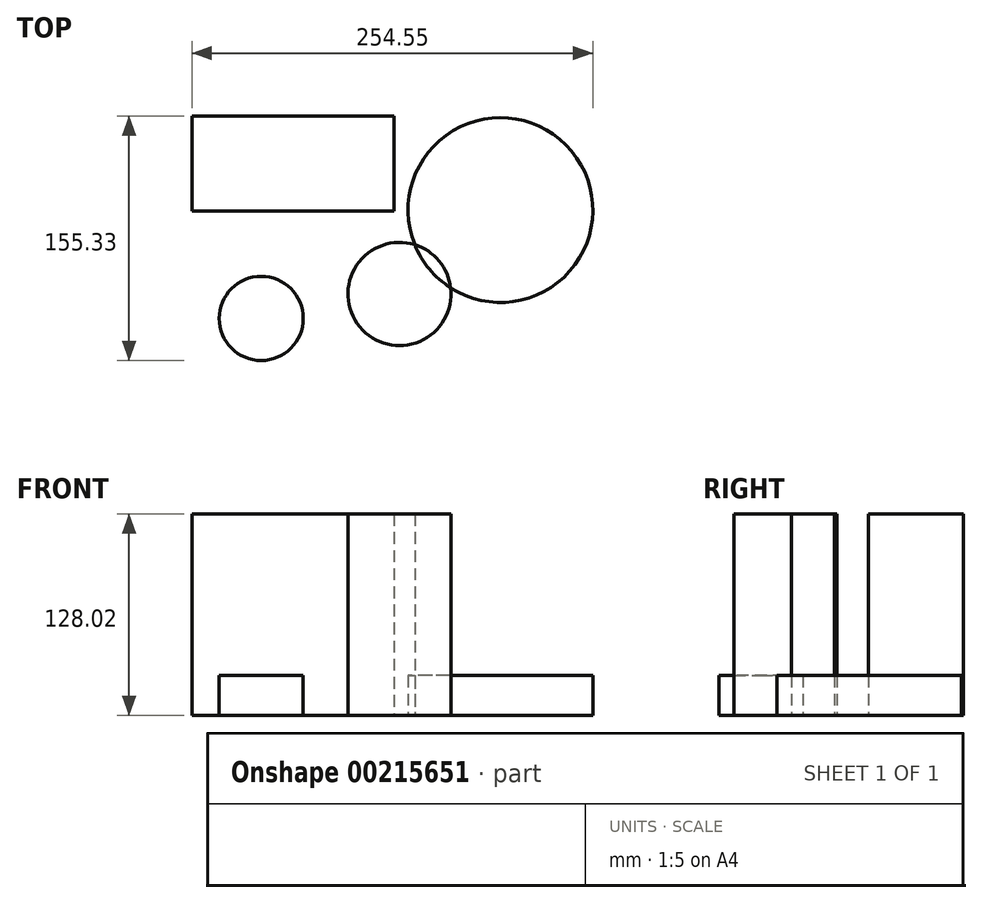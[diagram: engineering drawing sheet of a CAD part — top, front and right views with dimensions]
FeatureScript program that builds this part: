
annotation { "Feature Type Name" : "Feature", "Feature Type Description" : "" }
export const myFeature = defineFeature(function(context is Context, id is Id, definition is map)
    precondition{}
    {
        {
            var Q0;
            Q0=qCreatedBy(makeId("Top.planeOp"),FACE);
            var sketch = newSketch(context, id + "F0", { "sketchPlane" : qUnion([Q0])});
            skLineSegment(sketch, "E0.bottom", {"start": v(40.48, 26.16) * mm, "end": v(-87.82, 26.16) * mm});
            skLineSegment(sketch, "E0.top", {"start": v(40.48, 86.57) * mm, "end": v(-87.82, 86.57) * mm});
            skLineSegment(sketch, "E0.left", {"start": v(40.48, 26.16) * mm, "end": v(40.48, 86.57) * mm});
            skLineSegment(sketch, "E0.right", {"start": v(-87.82, 26.16) * mm, "end": v(-87.82, 86.57) * mm});
            skPoint(sketch, "E0.middle", {"position": v(-23.67, 56.36) * mm});
            skCircle(sketch, "E1", {"center": v(-43.9, -42.04) * mm, "radius": 26.72 * mm});
            skCircle(sketch, "E2", {"center": v(43.9, -26.47) * mm, "radius": 32.73 * mm});
            skCircle(sketch, "E3", {"center": v(108.06, 26.78) * mm, "radius": 58.67 * mm});
            skSolve(sketch);
        }
        {
            var Q0;
            Q0=makeQuery(id+"F0.imprint","IMPRINT",FACE,{"disambiguationData":[TD([[makeQuery(id+"F0.imprint","IMPRINT",EDGE,{"derivedFrom":sQuery(id+"F0.wireOp",EDGE,"E1")}),1.0]])]});
            var Q1;
            {var subQ0=sQuery(id+"F0.wireOp",EDGE,"E3");var subQ1=sQuery(id+"F0.wireOp",EDGE,"E2");var subQ2=makeQuery(id+"F0.imprint","INTERSECT",VERTEX,{"disambiguationData":[OD(0.0)],"derivedFrom":[subQ1,subQ0]});Q1=makeQuery(id+"F0.imprint","IMPRINT",FACE,{"disambiguationData":[TD([[makeQuery(id+"F0.imprint","IMPRINT",EDGE,{"disambiguationData":[TD([[subQ2,1.0]])],"derivedFrom":subQ1}),-1.0]])]});}
            extrude(context, id + "F1", {"entities" : qUnion([Q0, Q1]), "depth" : 25.4 * mm});
        }
        {
            var Q0;
            Q0=makeQuery(id+"F0.imprint","IMPRINT",FACE,{"disambiguationData":[TD([[makeQuery(id+"F0.imprint","IMPRINT",EDGE,{"derivedFrom":sQuery(id+"F0.wireOp",EDGE,"E0.bottom")}),-1.0]])]});
            var Q1;
            {var subQ0=sQuery(id+"F0.wireOp",EDGE,"E3");var subQ1=sQuery(id+"F0.wireOp",EDGE,"E2");var subQ2=makeQuery(id+"F0.imprint","INTERSECT",VERTEX,{"disambiguationData":[OD(0.0)],"derivedFrom":[subQ1,subQ0]});Q1=makeQuery(id+"F0.imprint","IMPRINT",FACE,{"disambiguationData":[TD([[makeQuery(id+"F0.imprint","IMPRINT",EDGE,{"disambiguationData":[TD([[subQ2,-1.0]])],"derivedFrom":subQ1}),1.0]])]});}
            extrude(context, id + "F2", {"entities" : qUnion([Q0, Q1]), "depth" : 128.02 * mm});
        }
    });
